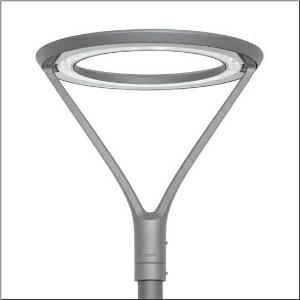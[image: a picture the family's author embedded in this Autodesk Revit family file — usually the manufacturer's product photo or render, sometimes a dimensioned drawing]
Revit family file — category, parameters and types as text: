
# Revit family: dl_r__20___p1_0a_5xa512836r008p_def9
name_source: partatom
category: Lighting Fixtures
units: mm (PartAtom-declared; Revit-internal decimal feet)

## family parameters
Cut with Voids When Loaded = No
Host = Face
Light Source = No
Part Type = Normal
Room Calculation Point = No
Round Connector Dimension = Use Diameter
Shared = No

## types (1)
- --- (1 x LED, 4220 lm, 40.6 W, 2700K)
    Apparent Load = 41 VA
    CIE Flux Codes = 31 71 96 100 100
    Color Rendering = 70
    Color Temperature = 2700K
    Default Elevation = 1800 mm
    Description = DL® 20, mast luminaire, primary light control with cycle path optic, highly specular, primary optical cover: cover, of toughened safety glass of clear glass with excellent transmission level, light distribution: P1.0a, light emission: direct distribution, primary light characteristic: asymmetric, installation type: post-top, LED, High Power LED, rated luminous flux: 4.220lm, luminous efficacy: 104lm/W, light colour: 727, colour temperature: 2700K, control gear: Plus, control: flexible luminous flux parameterisation, time-dependent luminous flux control, constant luminous flux control, digital communication interface, power reduction, overheat protection, electronic power reduction, mains connection: 220..240V, 50/60Hz, connection cable pre-assembled, cable length: 5m, start of lifetime: 41W, end of service life: 42W, reduction: 20W, luminaire housing, upper part, of cast aluminium, powder-coated, Siteco® metallic grey (DB 702S), diameter: 690mm, height: 690mm, spigot size: 76mm (post-top), mounting height: 4..6m, luminaire housing, of cast aluminium, powder-coated, Siteco® metallic grey (DB 702S), equipment: Power, protection rating (complete): IP66, insulation class (complete): insulation class II (safety insulation), certification: CE, ENEC, VDE, impact resistance: IK08, permissible operating ambient temperature: -25..+30°C, standard-compliant lighting for roads and squares, packaging unit: 1 piece

Light Distribution: P1.0a
    Height = 690 mm
    Lamp = 1 x LED
    Lamp Light Flux = 4220 lm
    Lamp Power = 40.6 W
    Lamp count = 1
    Length = 690 mm
    Luminous efficacy = 104 lm/W
    Manufacturer = Siteco
    ModVariant = No
    Model = 5XA512836R008P
    Number of Poles = 1
    OnlyDefault = Yes
    Power Factor = 1
    Product Name = DL® 20 | P1.0a
    Product group = mast luminaire | pylon top
    ProductGroupID = 6100
    Protection Class = Protection class II
    Protection Degree = IP 66
    RLX_Detail_Level = 1
    RLX_Emergency_Light_Flux = 0 lm
    RLX_Emergency_Type = 0
    RLX_Emergency_Type_DB = No
    RlxData = <blob elided: 207153 chars, md5=79e42144>
    Socket = socket
    Standby Power = 0 W
    System Light Flux = 4220 lm
    System Power = 41 W
    Type Comments = factory setting: luminous flux: 100 % | dim-lin: 254 | 549 mA
    Type Image = l_1006001.jpg
    URL = http://relux.com
    VarID = @adj_077050
    Voltage = 0 V
    Weight = 0.00 kg
    Width = 0 mm  [stored 0 ft]

note: [stored X ft] marks values corroborated as IEEE doubles in the binary element streams (Revit-internal decimal feet)

## geometry (parser evidence)
native form markers: Blend x4, Sweep x9
no freeform markers — native parametric forms only
